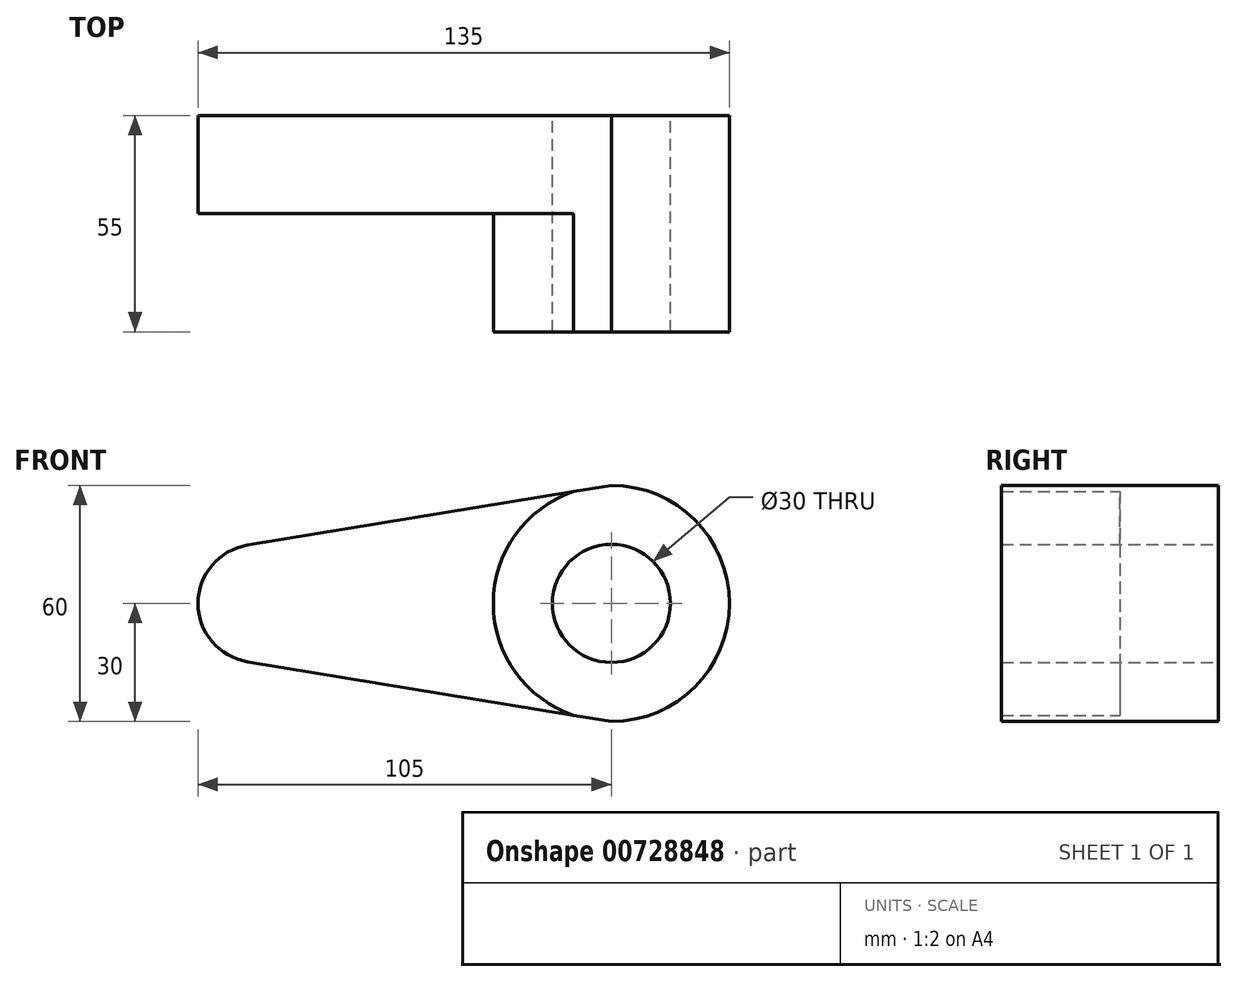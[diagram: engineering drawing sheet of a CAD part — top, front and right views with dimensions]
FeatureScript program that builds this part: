
annotation { "Feature Type Name" : "Feature", "Feature Type Description" : "" }
export const myFeature = defineFeature(function(context is Context, id is Id, definition is map)
    precondition{}
    {
        {
            var Q0;
            Q0=qCreatedBy(makeId("Front.planeOp"),FACE);
            var sketch = newSketch(context, id + "F0", { "sketchPlane" : qUnion([Q0])});
            skCircle(sketch, "E0", {"center": v(0, 0) * mm, "radius": 30 * mm});
            skCircle(sketch, "E1", {"center": v(0, 0) * mm, "radius": 15 * mm});
            skCircle(sketch, "E2", {"center": v(-90, 0) * mm, "radius": 15 * mm});
            skLineSegment(sketch, "E3", {"start": v(-92.43, 14.8) * mm, "end": v(0, 30) * mm});
            skLineSegment(sketch, "E4", {"start": v(-92.43, -14.8) * mm, "end": v(0, -30) * mm});
            skSolve(sketch);
        }
        {
            var Q0;
            {var subQ0=sQuery(id+"F0.wireOp",EDGE,"E2");var subQ1=makeQuery(id+"F0.imprint","INTERSECT",VERTEX,{"derivedFrom":[subQ0,sQuery(id+"F0.wireOp",EDGE,"E3")]});Q0=makeQuery(id+"F0.imprint","IMPRINT",FACE,{"disambiguationData":[TD([[makeQuery(id+"F0.imprint","IMPRINT",EDGE,{"disambiguationData":[TD([[subQ1,-1.0]])],"derivedFrom":subQ0}),1.0]])]});}
            var Q1;
            {var subQ0=sQuery(id+"F0.wireOp",EDGE,"E3");var subQ1=sQuery(id+"F0.wireOp",EDGE,"E0");var subQ2=makeQuery(id+"F0.imprint","INTERSECT",VERTEX,{"disambiguationData":[OD(1.0)],"derivedFrom":[subQ1,subQ0]});Q1=makeQuery(id+"F0.imprint","IMPRINT",FACE,{"disambiguationData":[TD([[makeQuery(id+"F0.imprint","IMPRINT",EDGE,{"disambiguationData":[TD([[subQ2,-1.0]])],"derivedFrom":subQ1}),-1.0]])]});}
            extrude(context, id + "F1", {"entities" : qUnion([Q0, Q1]), "depth" : 25 * mm, "offsetDistance" : 25 * mm});
        }
        {
            var Q0;
            Q0=makeQuery(id+"F0.imprint","IMPRINT",FACE,{"disambiguationData":[TD([[makeQuery(id+"F0.imprint","IMPRINT",EDGE,{"derivedFrom":sQuery(id+"F0.wireOp",EDGE,"E1")}),-1.0]])]});
            extrude(context, id + "F2", {"entities" : qUnion([Q0]), "operationType" : NewBodyOperationType.ADD, "depth" : 55 * mm, "offsetDistance" : 25 * mm});
        }
    });
